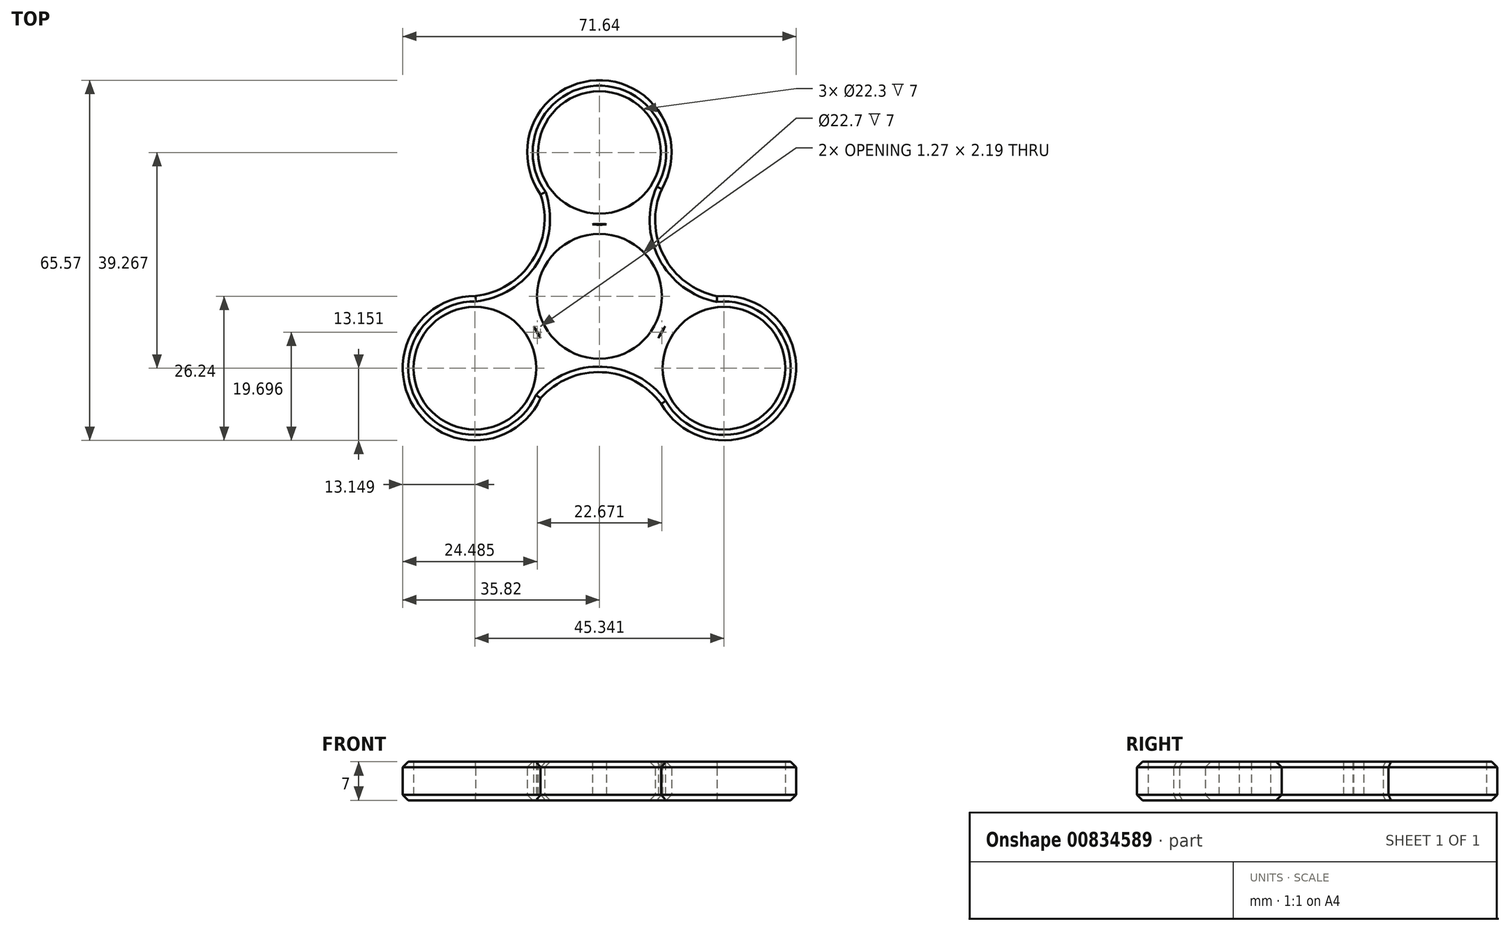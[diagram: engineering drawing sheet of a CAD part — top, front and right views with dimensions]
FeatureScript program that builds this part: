
annotation { "Feature Type Name" : "Feature", "Feature Type Description" : "" }
export const myFeature = defineFeature(function(context is Context, id is Id, definition is map)
    precondition{}
    {
        {
            var Q0;
            Q0=qCreatedBy(makeId("Top.planeOp"),FACE);
            var sketch = newSketch(context, id + "F0", { "sketchPlane" : qUnion([Q0])});
            skCircle(sketch, "E0", {"center": v(0, 0) * mm, "radius": 11.35 * mm});
            skArc(sketch, "E1", {"start": v(1.27, 13.09) * mm, "mid": v(0, 13.15) * mm, "end": v(-1.27, 13.09) * mm});
            skCircle(sketch, "E2", {"center": v(0, 26.18) * mm, "radius": 11.15 * mm});
            skArc(sketch, "E3", {"start": v(11.34, 19.51) * mm, "mid": v(-0.58, 39.31) * mm, "end": v(-10.7, 18.54) * mm});
            skArc(sketch, "E4.1.0", {"start": v(-10.7, -7.64) * mm, "mid": v(-11.28, -6.51) * mm, "end": v(-11.97, -5.45) * mm});
            skCircle(sketch, "E4.1.1", {"center": v(-22.67, -13.09) * mm, "radius": 11.15 * mm});
            skArc(sketch, "E4.2.0", {"start": v(11.23, -19.57) * mm, "mid": v(34.34, -19.15) * mm, "end": v(21.4, 0) * mm});
            skCircle(sketch, "E4.2.1", {"center": v(22.67, -13.09) * mm, "radius": 11.15 * mm});
            skArc(sketch, "E5", {"start": v(11.34, 19.51) * mm, "mid": v(11.71, 7.35) * mm, "end": v(21.4, 0) * mm});
            skArc(sketch, "E6.1.0", {"start": v(-22.57, 0.06) * mm, "mid": v(-12.23, 6.47) * mm, "end": v(-10.7, 18.54) * mm});
            skArc(sketch, "E6.2.0", {"start": v(11.23, -19.57) * mm, "mid": v(0.51, -13.82) * mm, "end": v(-10.7, -18.54) * mm});
            skArc(sketch, "E7.trimOffspring", {"start": v(-1.27, 13.09) * mm, "mid": v(0, 13.03) * mm, "end": v(1.27, 13.09) * mm});
            skArc(sketch, "E8.trimOffspring", {"start": v(10.7, -7.64) * mm, "mid": v(11.39, -6.58) * mm, "end": v(11.97, -5.45) * mm});
            skArc(sketch, "E9.trimOffspring", {"start": v(-11.97, -5.45) * mm, "mid": v(-11.39, -6.58) * mm, "end": v(-10.7, -7.64) * mm});
            skArc(sketch, "E10.trimOffspring", {"start": v(-22.57, 0.06) * mm, "mid": v(-33.76, -20.16) * mm, "end": v(-10.7, -18.54) * mm});
            skArc(sketch, "E11.trimOffspring", {"start": v(11.97, -5.45) * mm, "mid": v(11.28, -6.51) * mm, "end": v(10.7, -7.64) * mm});
            skSolve(sketch);
        }
        {
            var Q0;
            Q0=makeQuery(id+"F0.imprint","IMPRINT",FACE,{"disambiguationData":[TD([[makeQuery(id+"F0.imprint","IMPRINT",EDGE,{"derivedFrom":sQuery(id+"F0.wireOp",EDGE,"E0")}),-1.0]])]});
            extrude(context, id + "F1", {"entities" : qUnion([Q0]), "depth" : 7 * mm, "offsetDistance" : 25 * mm});
        }
        {
            var Q0;
            Q0=makeQuery(id+"F1.opExtrude","CAP_EDGE",EDGE,{"disambiguationData":[OSD([sQuery(id+"F0.wireOp",EDGE,"E6.2.0")])],"isStart":false});
            var Q1;
            Q1=makeQuery(id+"F1.opExtrude","CAP_EDGE",EDGE,{"disambiguationData":[OSD([sQuery(id+"F0.wireOp",EDGE,"E10.trimOffspring")])],"isStart":false});
            var Q2;
            Q2=makeQuery(id+"F1.opExtrude","CAP_EDGE",EDGE,{"disambiguationData":[OSD([sQuery(id+"F0.wireOp",EDGE,"E6.1.0")])],"isStart":false});
            var Q3;
            Q3=makeQuery(id+"F1.opExtrude","CAP_EDGE",EDGE,{"disambiguationData":[OSD([sQuery(id+"F0.wireOp",EDGE,"E3")])],"isStart":false});
            var Q4;
            Q4=makeQuery(id+"F1.opExtrude","CAP_EDGE",EDGE,{"disambiguationData":[OSD([sQuery(id+"F0.wireOp",EDGE,"E5")])],"isStart":false});
            var Q5;
            Q5=makeQuery(id+"F1.opExtrude","CAP_EDGE",EDGE,{"disambiguationData":[OSD([sQuery(id+"F0.wireOp",EDGE,"E4.2.0")])],"isStart":false});
            var Q6;
            Q6=makeQuery(id+"F1.opExtrude","CAP_EDGE",EDGE,{"disambiguationData":[OSD([sQuery(id+"F0.wireOp",EDGE,"E4.2.0")])],"isStart":true});
            var Q7;
            Q7=makeQuery(id+"F1.opExtrude","CAP_EDGE",EDGE,{"disambiguationData":[OSD([sQuery(id+"F0.wireOp",EDGE,"E6.2.0")])],"isStart":true});
            var Q8;
            Q8=makeQuery(id+"F1.opExtrude","CAP_EDGE",EDGE,{"disambiguationData":[OSD([sQuery(id+"F0.wireOp",EDGE,"E10.trimOffspring")])],"isStart":true});
            var Q9;
            Q9=makeQuery(id+"F1.opExtrude","CAP_EDGE",EDGE,{"disambiguationData":[OSD([sQuery(id+"F0.wireOp",EDGE,"E5")])],"isStart":true});
            var Q10;
            Q10=makeQuery(id+"F1.opExtrude","CAP_EDGE",EDGE,{"disambiguationData":[OSD([sQuery(id+"F0.wireOp",EDGE,"E3")])],"isStart":true});
            var Q11;
            Q11=makeQuery(id+"F1.opExtrude","CAP_EDGE",EDGE,{"disambiguationData":[OSD([sQuery(id+"F0.wireOp",EDGE,"E6.1.0")])],"isStart":true});
            chamfer(context, id + "F2", {"entities" : qUnion([Q0, Q1, Q2, Q3, Q4, Q5, Q6, Q7, Q8, Q9, Q10, Q11]), "width" : 1 * mm, "tangentPropagation" : true});
        }
    });
